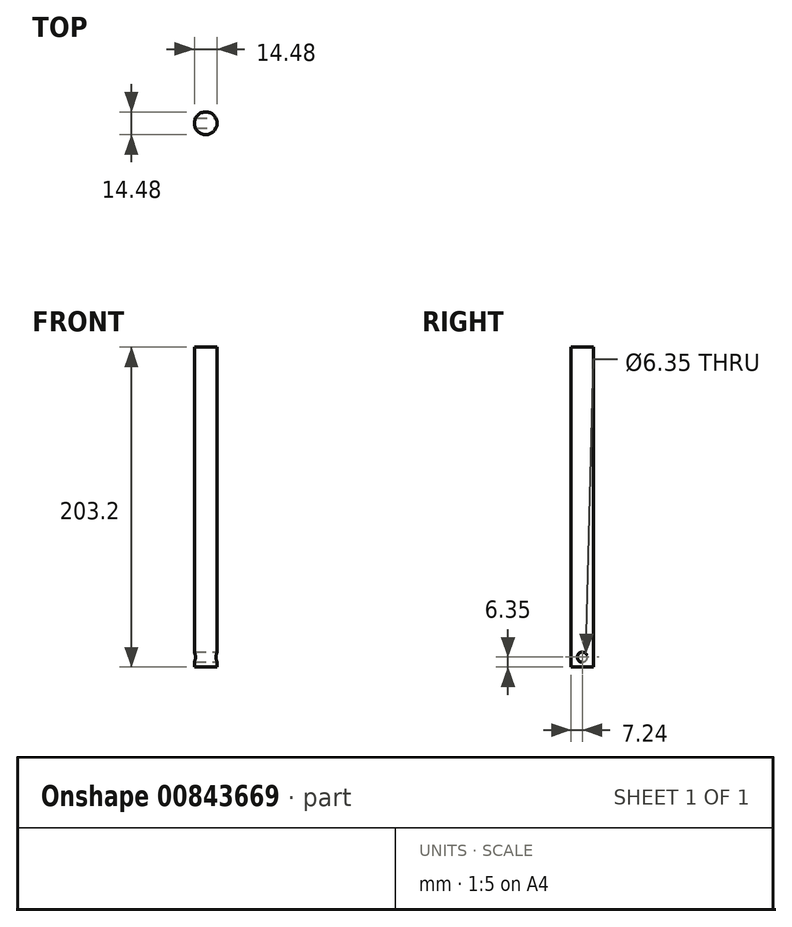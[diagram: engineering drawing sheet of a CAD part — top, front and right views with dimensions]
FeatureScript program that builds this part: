
annotation { "Feature Type Name" : "Feature", "Feature Type Description" : "" }
export const myFeature = defineFeature(function(context is Context, id is Id, definition is map)
    precondition{}
    {
        {
            var Q0;
            Q0=qCreatedBy(makeId("Top.planeOp"),FACE);
            var sketch = newSketch(context, id + "F0", { "sketchPlane" : qUnion([Q0])});
            skCircle(sketch, "E0", {"center": v(0, 0) * mm, "radius": 7.24 * mm});
            skSolve(sketch);
        }
        {
            var Q0;
            Q0=qSketchRegion(id+"F0",true);
            extrude(context, id + "F1", {"entities" : qUnion([Q0]), "depth" : 203.2 * mm, "offsetDistance" : 25.4 * mm});
        }
        {
            var Q0;
            Q0=qCreatedBy(makeId("Right.planeOp"),FACE);
            var sketch = newSketch(context, id + "F2", { "sketchPlane" : qUnion([Q0])});
            skCircle(sketch, "E1", {"center": v(0, 6.35) * mm, "radius": 3.18 * mm});
            skSolve(sketch);
        }
        {
            var Q0;
            Q0=qSketchRegion(id+"F2",true);
            extrude(context, id + "F3", {"entities" : qUnion([Q0]), "operationType" : NewBodyOperationType.REMOVE, "oppositeDirection" : true, "depth" : 25.4 * mm, "offsetDistance" : 25.4 * mm, "hasSecondDirection" : true, "secondDirectionOppositeDirection" : false, "secondDirectionDepth" : 25.4 * mm});
        }
    });
